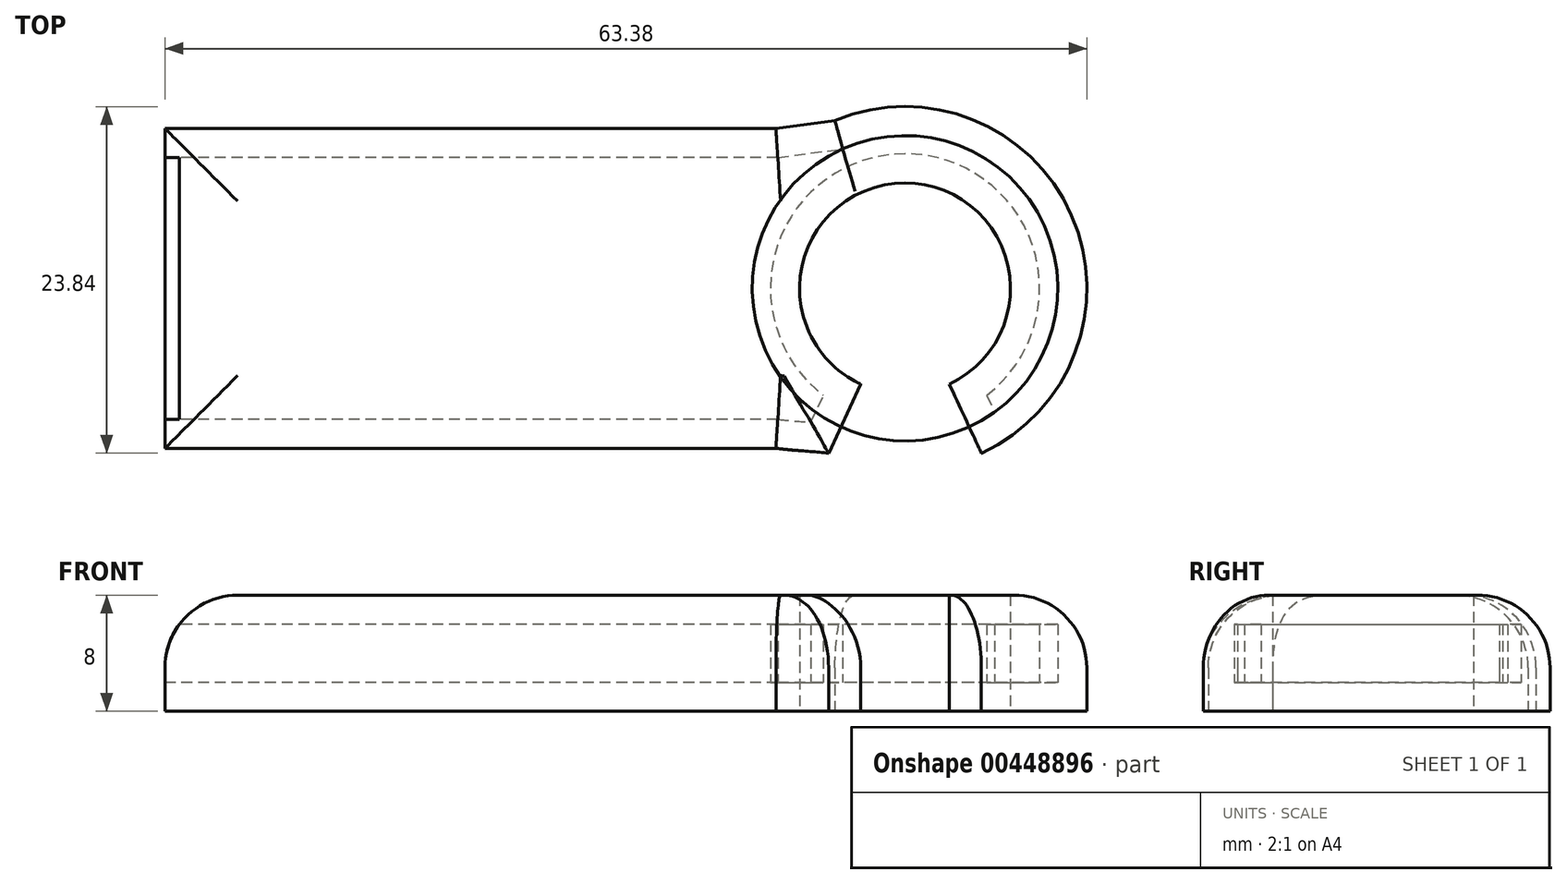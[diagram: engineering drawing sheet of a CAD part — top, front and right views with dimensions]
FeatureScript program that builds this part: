
annotation { "Feature Type Name" : "Feature", "Feature Type Description" : "" }
export const myFeature = defineFeature(function(context is Context, id is Id, definition is map)
    precondition{}
    {
        {
            var Q0;
            Q0=qCreatedBy(makeId("Top.planeOp"),FACE);
            var sketch = newSketch(context, id + "F0", { "sketchPlane" : qUnion([Q0])});
            skLineSegment(sketch, "E0.bottom", {"start": v(21, 11) * mm, "end": v(-21, 11) * mm});
            skLineSegment(sketch, "E0.top", {"start": v(21, -11) * mm, "end": v(-21, -11) * mm});
            skLineSegment(sketch, "E0.right", {"start": v(-21, 11) * mm, "end": v(-21, -11) * mm});
            skPoint(sketch, "E0.middle", {"position": v(0, 0) * mm});
            skPoint(sketch, "E1", {"position": v(21, 0) * mm});
            skPoint(sketch, "E2", {"position": v(36, 0) * mm});
            skArc(sketch, "E3", {"start": v(35.13, -11.34) * mm, "mid": v(41.32, 5.03) * mm, "end": v(25.06, 11.53) * mm});
            skPoint(sketch, "E4", {"position": v(21, 11) * mm});
            skPoint(sketch, "E5", {"position": v(21, -11) * mm});
            skFitSpline(sketch, "E6", {"points": [v(21, 11) * mm, v(25.06, 11.53) * mm], "startDerivative": vector(4.06, 0.53) * mm, "endDerivative": vector(4.06, 0.53) * mm});
            skFitSpline(sketch, "E7", {"points": [v(21, -11) * mm, v(24.63, -11.34) * mm], "startDerivative": vector(4.06, -0.53) * mm, "endDerivative": vector(4.06, -0.53) * mm});
            skPoint(sketch, "E8", {"position": v(35.13, -11.34) * mm});
            skLineSegment(sketch, "E9", {"start": v(24.63, -11.34) * mm, "end": v(35.13, -11.34) * mm});
            skCircle(sketch, "E10", {"center": v(29.88, 0) * mm, "radius": 7.25 * mm});
            skLineSegment(sketch, "E11", {"start": v(24.63, -11.34) * mm, "end": v(29.88, 0) * mm});
            skLineSegment(sketch, "E12", {"start": v(29.88, 0) * mm, "end": v(35.13, -11.34) * mm});
            skSolve(sketch);
        }
        {
            var Q0;
            Q0=makeQuery(id+"F0.imprint","IMPRINT",FACE,{"disambiguationData":[TD([[makeQuery(id+"F0.imprint","IMPRINT",EDGE,{"derivedFrom":sQuery(id+"F0.wireOp",EDGE,"E0.bottom")}),1.0]])]});
            extrude(context, id + "F1", {"entities" : qUnion([Q0]), "depth" : 8 * mm});
        }
        {
            var Q0;
            Q0=makeQuery(id+"F1.opExtrude","SWEPT_FACE",FACE,{"disambiguationData":[OSD([sQuery(id+"F0.wireOp",EDGE,"E0.right")])]});
            shell(context, id + "F2", {"entities" : qUnion([Q0]), "thickness" : 2 * mm});
        }
        {
            var Q0;
            Q0=makeQuery(id+"F1.opExtrude","CAP_EDGE",EDGE,{"disambiguationData":[OSD([sQuery(id+"F0.wireOp",EDGE,"E3")])],"isStart":false});
            var Q1;
            Q1=makeQuery(id+"F1.opExtrude","CAP_EDGE",EDGE,{"disambiguationData":[OSD([sQuery(id+"F0.wireOp",EDGE,"E11")])],"isStart":false});
            var Q2;
            Q2=makeQuery(id+"F1.opExtrude","CAP_EDGE",EDGE,{"disambiguationData":[OSD([sQuery(id+"F0.wireOp",EDGE,"E7")])],"isStart":false});
            var Q3;
            Q3=makeQuery(id+"F1.opExtrude","CAP_EDGE",EDGE,{"disambiguationData":[OSD([sQuery(id+"F0.wireOp",EDGE,"E0.top")])],"isStart":false});
            var Q4;
            Q4=makeQuery(id+"F1.opExtrude","CAP_EDGE",EDGE,{"disambiguationData":[OSD([sQuery(id+"F0.wireOp",EDGE,"E0.right")])],"isStart":false});
            var Q5;
            Q5=makeQuery(id+"F1.opExtrude","CAP_EDGE",EDGE,{"disambiguationData":[OSD([sQuery(id+"F0.wireOp",EDGE,"E0.bottom")])],"isStart":false});
            var Q6;
            Q6=makeQuery(id+"F1.opExtrude","CAP_EDGE",EDGE,{"disambiguationData":[OSD([sQuery(id+"F0.wireOp",EDGE,"E6")])],"isStart":false});
            fillet(context, id + "F3", {"entities" : qUnion([Q0, Q1, Q2, Q3, Q4, Q5, Q6]), "radius" : 5 * mm, "tangentPropagation" : true, "allowEdgeOverflow" : false});
        }
    });
